# Revit family: 581b5368-f68a-495b-8b41-31392ea5a164
name_source: partatom
category: Plumbing Fixtures
revit_build: Autodesk Revit 2016 (Build: 20161004_0715(x64)
units: mm (PartAtom-declared; Revit-internal decimal feet)

## family parameters
Cut with Voids When Loaded = No
Host = Face
OmniClass Number = 23.45.55.17
OmniClass Title = Mixing Faucets
Part Type = Normal
Room Calculation Point = No
Round Connector Dimension = Use Diameter
Shared = No

## types (1)
- SV230
    Assembly Code = C1030210
    CW Connection = No
    CWFU = 0
    Cold Water Connector = Connector for Cold Water In
    Default Elevation = 4' - 0"
    Description = Ligature Resistant Shower Handle, Escutcheon Plate & Valve
    Finish = Metal - BSP - Chrome - Polished
    HW Connection = No
    HWFU = 0
    Hot Water Connector = Connector for Hot Water In
    Manufacturer = Behavioral Safety Products
    Model = SV230
    Product Documentation Link = http://besafeprod.com
    Product Page URL = http://besafeprod.com
    Product data url = https://bimobject.com
    Type Image = <None>
    URL = http://besafeprod.com
    Vent Connection = No
    Waste Connection = No
    Water Out Connector 1 = Connector For Water Out 1
    Water Out Connector 2 = Connector For Water Out 2

## geometry (parser evidence)
native form markers: Blend x15, Sweep x9
no freeform markers — native parametric forms only
